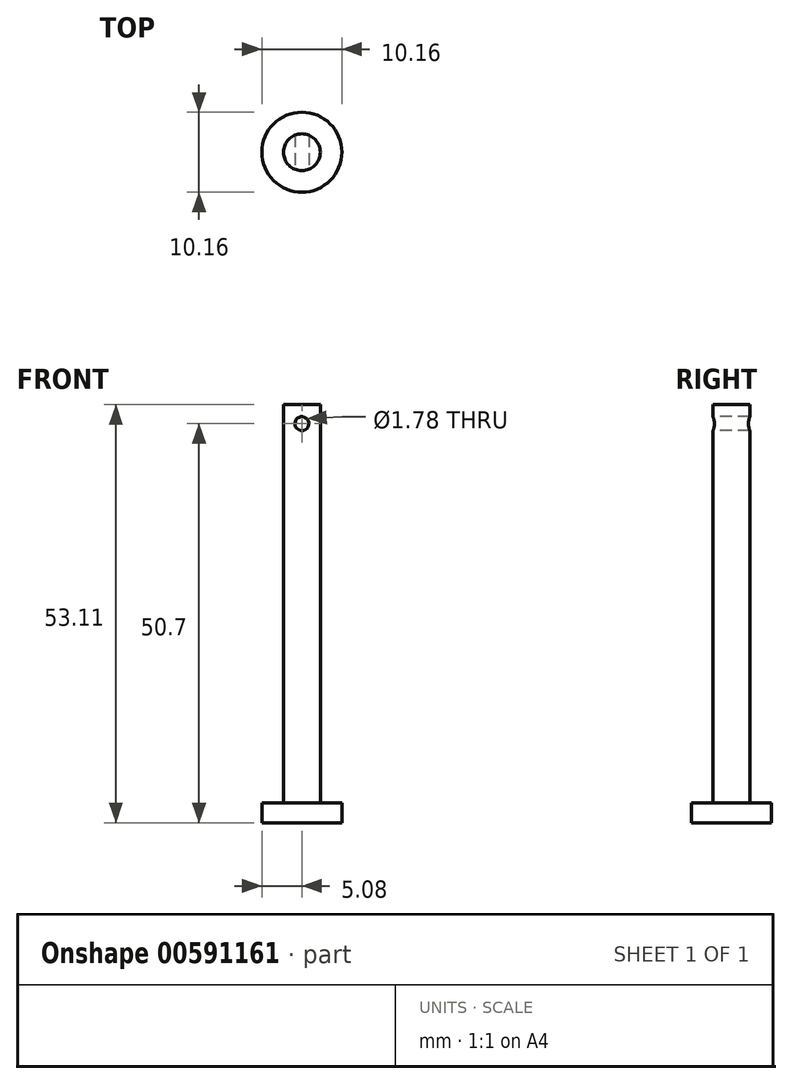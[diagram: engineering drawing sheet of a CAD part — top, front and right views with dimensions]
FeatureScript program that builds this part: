
annotation { "Feature Type Name" : "Feature", "Feature Type Description" : "" }
export const myFeature = defineFeature(function(context is Context, id is Id, definition is map)
    precondition{}
    {
        {
            var Q0;
            Q0=qCreatedBy(makeId("Top.planeOp"),FACE);
            var sketch = newSketch(context, id + "F0", { "sketchPlane" : qUnion([Q0])});
            skCircle(sketch, "E0", {"center": v(0, 0) * mm, "radius": 2.33 * mm});
            skSolve(sketch);
        }
        {
            var Q0;
            Q0=makeQuery(id+"F0.imprint","IMPRINT",FACE,{"disambiguationData":[TD([[makeQuery(id+"F0.imprint","IMPRINT",EDGE,{"derivedFrom":sQuery(id+"F0.wireOp",EDGE,"E0")}),1.0]])]});
            extrude(context, id + "F1", {"entities" : qUnion([Q0]), "depth" : 50.57 * mm, "offsetDistance" : 25.4 * mm});
        }
        {
            var Q0;
            Q0=makeQuery(id+"F1.opExtrude","CAP_FACE",FACE,{"disambiguationData":[OSD([sQuery(id+"F0.wireOp",EDGE,"E0")])],"isStart":true});
            var sketch = newSketch(context, id + "F2", { "sketchPlane" : qUnion([Q0])});
            skCircle(sketch, "E1", {"center": v(0, 0) * mm, "radius": 5.08 * mm});
            skSolve(sketch);
        }
        {
            var Q0;
            Q0=makeQuery(id+"F2.imprint","IMPRINT",FACE,{"disambiguationData":[TD([[makeQuery(id+"F2.imprint","IMPRINT",EDGE,{"derivedFrom":sQuery(id+"F2.wireOp",EDGE,"E1")}),1.0]])]});
            var Q1;
            Q1=makeQuery(id+"F2.imprint","IMPRINT",FACE,{"disambiguationData":[TD([[makeQuery(id+"F2.imprint","IMPRINT",EDGE,{"derivedFrom":makeQuery(id+"F1.opExtrude","CAP_EDGE",EDGE,{"disambiguationData":[OSD([sQuery(id+"F0.wireOp",EDGE,"E0")])],"isStart":true})}),-1.0]])]});
            extrude(context, id + "F3", {"entities" : qUnion([Q0, Q1]), "operationType" : NewBodyOperationType.ADD, "depth" : 2.54 * mm, "offsetDistance" : 25.4 * mm});
        }
        {
            var Q0;
            Q0=qCreatedBy(makeId("Front.planeOp"),FACE);
            var sketch = newSketch(context, id + "F4", { "sketchPlane" : qUnion([Q0])});
            skCircle(sketch, "E2", {"center": v(0, 48.16) * mm, "radius": 0.89 * mm});
            skSolve(sketch);
        }
        {
            var Q0;
            Q0 = qSketchRegion(id + "F4", true);
            extrude(context, id + "F5", {"entities" : qUnion([Q0]), "operationType" : NewBodyOperationType.REMOVE, "oppositeDirection" : true, "depth" : 25.4 * mm, "offsetDistance" : 25.4 * mm, "symmetric" : true});
        }
    });
